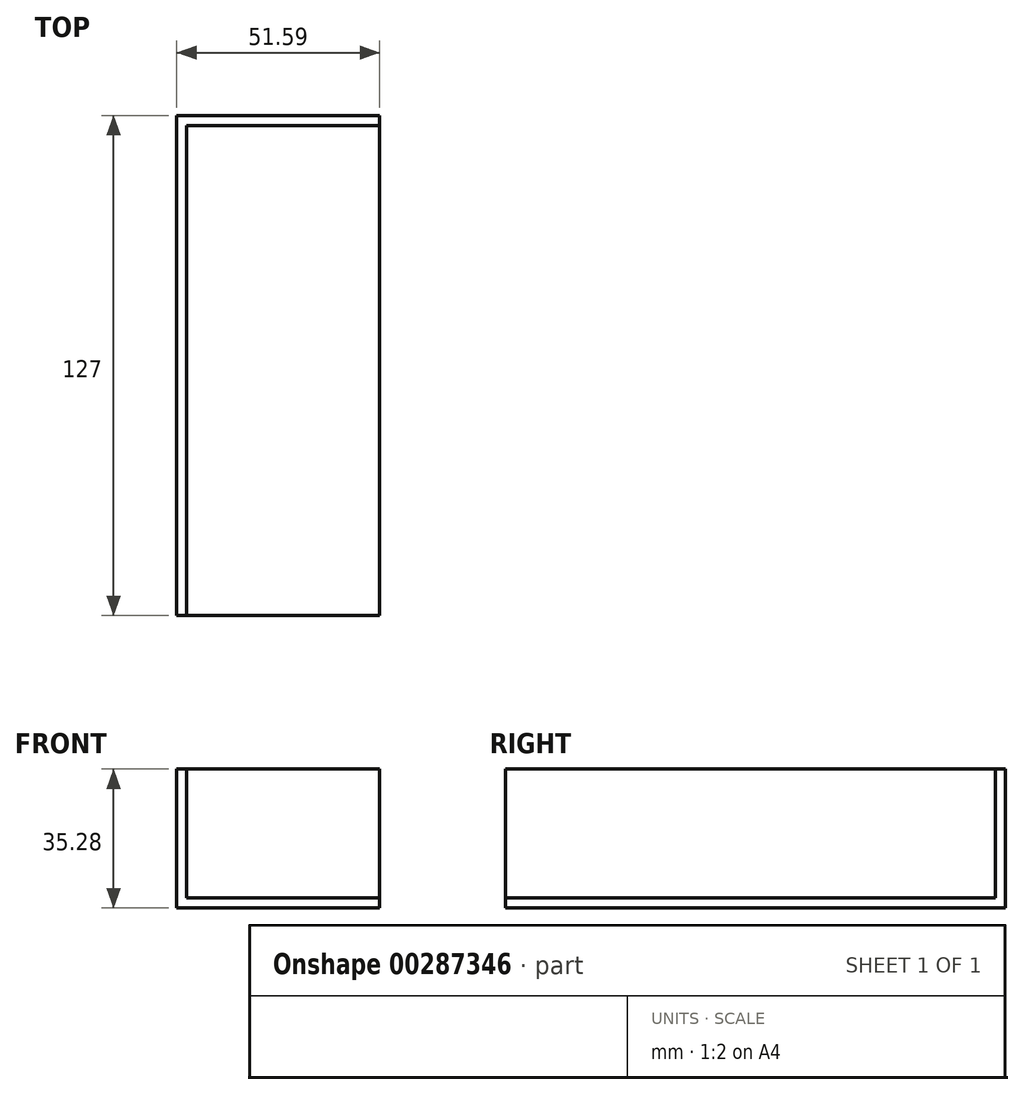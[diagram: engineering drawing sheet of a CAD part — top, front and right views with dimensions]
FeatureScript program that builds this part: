
annotation { "Feature Type Name" : "Feature", "Feature Type Description" : "" }
export const myFeature = defineFeature(function(context is Context, id is Id, definition is map)
    precondition{}
    {
        {
            var Q0;
            Q0=qCreatedBy(makeId("Front.planeOp"),FACE);
            var sketch = newSketch(context, id + "F0", { "sketchPlane" : qUnion([Q0])});
            skLineSegment(sketch, "E0.bottom", {"start": v(0, 0) * mm, "end": v(51.59, 0) * mm});
            skLineSegment(sketch, "E0.top", {"start": v(0, 35.28) * mm, "end": v(51.59, 35.28) * mm});
            skLineSegment(sketch, "E0.left", {"start": v(0, 0) * mm, "end": v(0, 35.28) * mm});
            skLineSegment(sketch, "E0.right", {"start": v(51.59, 0) * mm, "end": v(51.59, 35.28) * mm});
            skSolve(sketch);
        }
        {
            var Q0;
            Q0 = qSketchRegion(id + "F0", true);
            extrude(context, id + "F1", {"entities" : qUnion([Q0]), "depth" : 127 * mm});
        }
        {
            var Q0;
            Q0=makeQuery(id+"F1.opExtrude","CAP_FACE",FACE,{"disambiguationData":[OSD([sQuery(id+"F0.wireOp",EDGE,"E0.bottom"),sQuery(id+"F0.wireOp",EDGE,"E0.top"),sQuery(id+"F0.wireOp",EDGE,"E0.left"),sQuery(id+"F0.wireOp",EDGE,"E0.right")])],"isStart":false});
            var Q1;
            Q1=makeQuery(id+"F1.opExtrude","SWEPT_FACE",FACE,{"disambiguationData":[OSD([sQuery(id+"F0.wireOp",EDGE,"E0.top")])]});
            var Q2;
            Q2=makeQuery(id+"F1.opExtrude","SWEPT_FACE",FACE,{"disambiguationData":[OSD([sQuery(id+"F0.wireOp",EDGE,"E0.right")])]});
            shell(context, id + "F2", {"entities" : qUnion([Q0, Q1, Q2]), "thickness" : 2.54 * mm});
        }
    });
